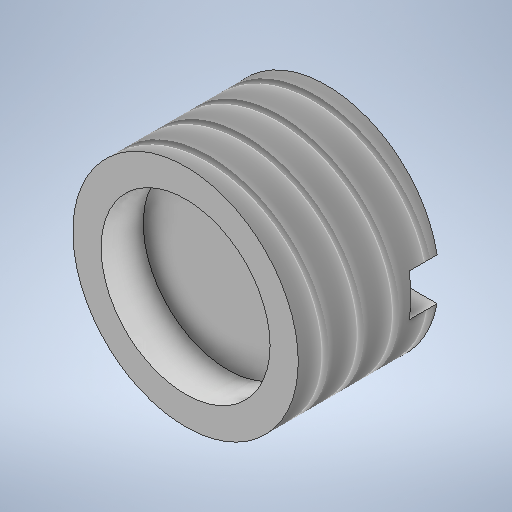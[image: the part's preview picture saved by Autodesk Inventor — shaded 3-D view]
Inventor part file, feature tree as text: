
AUTODESK INVENTOR PART (.ipt)
format: ipt  version: 2025.1 (Build 291241000, 241)  size: 293,376 bytes
history: native  units: mm
features: sketch x3, revolve x1, extrude x1, hole x1, thread x1, projected_geometry x1
ambient origin geometry x8: Origin, YZ Plane, XZ Plane, XY Plane, X Axis, Y Axis, Z Axis, Center Point
bodies: Solid1 (feature_tree)
feature tree (8):
  revolve  "Revolution1"  [1 undecoded]
  extrude  "Extrusion1"  Depth=0.75mm
  hole  "Hole1"  [1 undecoded]
  thread  "Thread1"  [1 undecoded]
  sketch  "Sketch1"  dims[d0=5.0mm d1=8.0mm]
  sketch  "Sketch2"  dims[d2=90.0deg d3=0.75mm]
  projected_geometry  "Projected Loop1"
  sketch  "Sketch3"  dims[d4=0.75mm d5=1.0mm d6=0.0mm d7=6.0mm d8=6.0mm d9=4.0mm d10=2.0mm d11=90.0deg d12=1.5mm d13=0.0mm d14=10.0mm d15=0.0mm]
note: 3 required parameter values undecoded (feature->parameter linkage not recoverable at this tier; creation-order binding heuristic only, values carry confidence <= 0.55)